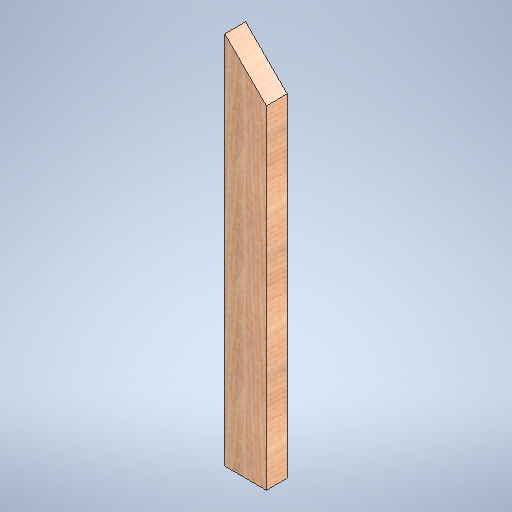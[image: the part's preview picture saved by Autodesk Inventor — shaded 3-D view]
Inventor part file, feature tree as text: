
AUTODESK INVENTOR PART (.ipt)
format: ipt  version: 2025 (Build 290162000, 162)  size: 325,120 bytes
history: native  units: in
note: dims shown in document units (in); Inventor stores cm internally (conversion verified against a paired STEP export)
features: extrude x1, sketch x1
ambient origin geometry x8: Origin, YZ Plane, XZ Plane, XY Plane, X Axis, Y Axis, Z Axis, Center Point
bodies: Solid1 (feature_tree)
feature tree (2):
  extrude  "Extrusion1"  Depth=2.0in TaperAngle=0.0deg
  sketch  "Sketch1"  dims[d1=36.0in d3=2.0in d4=0.0in]
